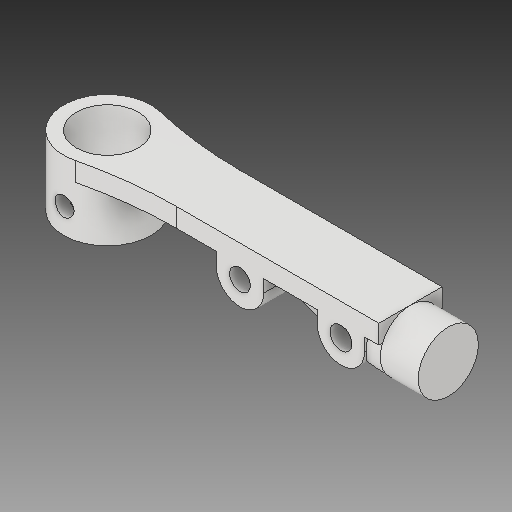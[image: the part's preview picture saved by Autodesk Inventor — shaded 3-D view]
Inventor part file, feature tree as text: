
AUTODESK INVENTOR PART (.ipt)
format: ipt  version: 2018.2 (Build 222227000, 227)  size: 242,688 bytes
history: native  units: mm
features: sketch x6, extrude x6, plane x1, loft x1, projected_geometry x1
ambient origin geometry x8: Origin, YZ Plane, XZ Plane, XY Plane, X Axis, Y Axis, Z Axis, Center Point
bodies: Solid1 (feature_tree)
feature tree (15):
  sketch  "Sketch1"  dims[d0=9.525mm d1=0.15mm]
  extrude  "Extrusion1"  Depth=0.15mm
  extrude  "Extrusion2"  Depth=3.0mm TaperAngle=0.0deg
  extrude  "Extrusion3"  Depth=16.0mm
  sketch  "Sketch3"  dims[d6=8.0mm d7=0.0mm d9=16.0mm]
  plane  "Work Plane1"
  loft  "Loft1"
  extrude  "Extrusion4"  Depth=10.0mm TaperAngle=90.0deg
  sketch  "Sketch10"  dims[d18=10.0mm d19=90.0deg d20=6.0mm d21=3.0mm d23=6.0mm d24=0.0mm d41=3.5mm d42=3.3mm d43=2.0mm d45=16.0mm d46=6.0mm d47=3.0mm d48=0.0mm d49=10.0mm d50=48.0mm d51=32.0mm d52=2.0mm d53=3.0mm d54=0.0mm]
  extrude  "Extrusion8"  Depth=6.0mm
  extrude  "Extrusion9"  Depth=3.0mm
  sketch  "Sketch2"  dims[d2=2.0mm d4=3.0mm d5=0.0mm]
  projected_geometry  "Projected Loop1"
  sketch  "Sketch5"  dims[d10=9.525mm d13=6.0mm d14=0.0mm]
  sketch  "Sketch6"  dims[d15=-24.0mm d16=10.0mm d17=90.0deg]
